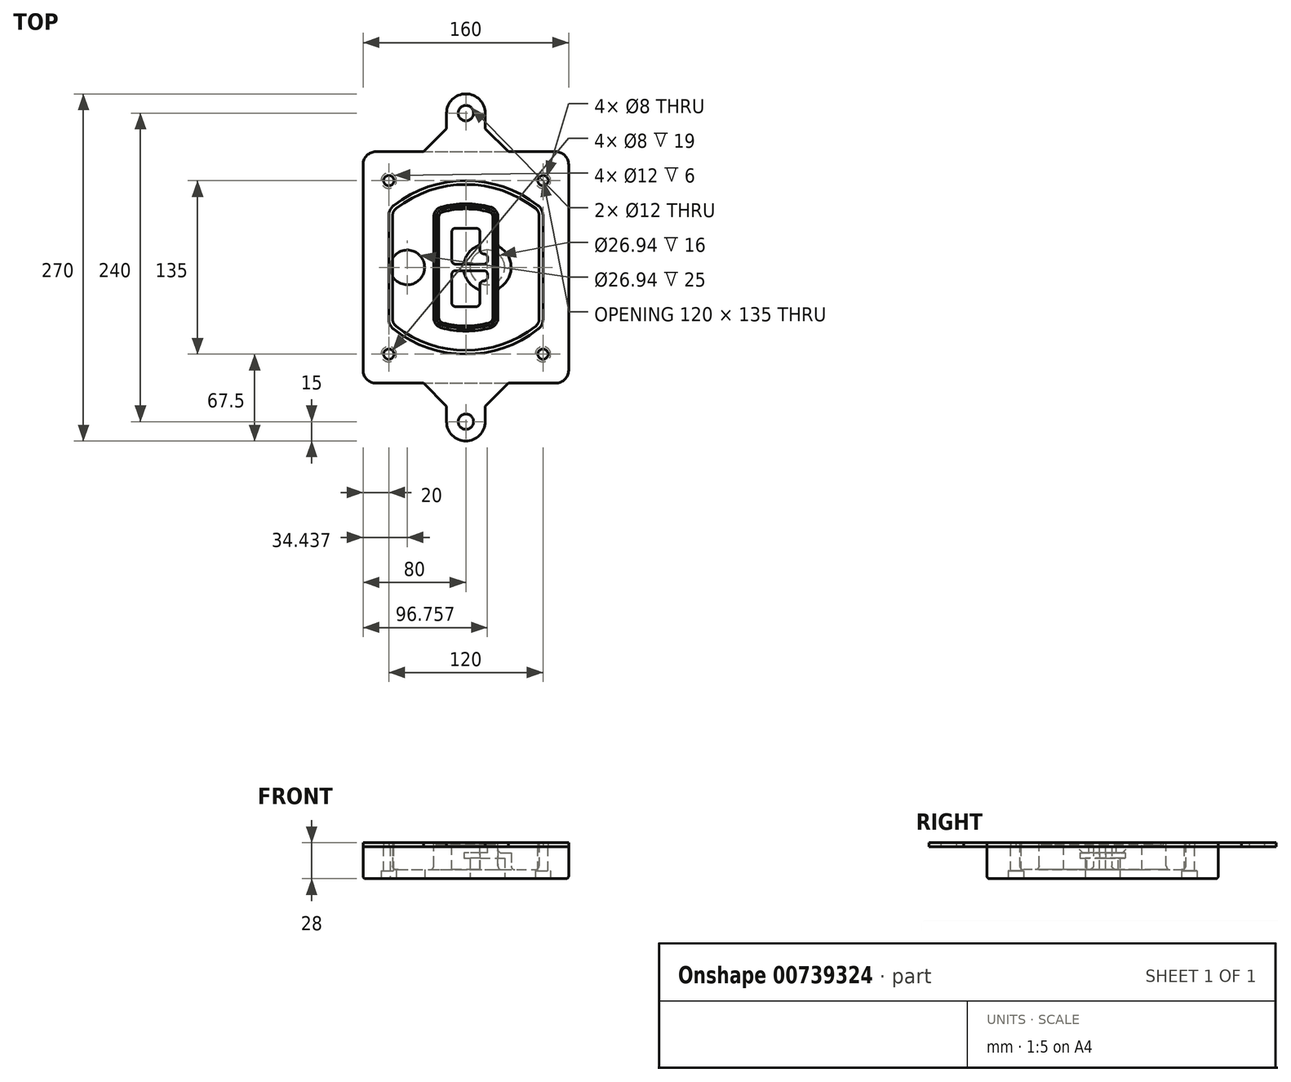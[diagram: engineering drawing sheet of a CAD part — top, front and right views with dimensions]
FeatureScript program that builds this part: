
annotation { "Feature Type Name" : "Feature", "Feature Type Description" : "" }
export const myFeature = defineFeature(function(context is Context, id is Id, definition is map)
    precondition{}
    {
        {
            var Q0;
            Q0=qCreatedBy(makeId("Top.planeOp"),FACE);
            var sketch = newSketch(context, id + "F0", { "sketchPlane" : qUnion([Q0])});
            skPoint(sketch, "E0.rect.middle", {"position": v(0, 0) * mm});
            skLineSegment(sketch, "E1.bottom", {"start": v(-70, -90) * mm, "end": v(70, -90) * mm});
            skLineSegment(sketch, "E1.top", {"start": v(-70, 90) * mm, "end": v(70, 90) * mm});
            skLineSegment(sketch, "E1.left", {"start": v(-80, -80) * mm, "end": v(-80, 80) * mm});
            skLineSegment(sketch, "E1.right", {"start": v(80, -80) * mm, "end": v(80, 80) * mm});
            skLineSegment(sketch, "E2", {"start": v(-80, 90) * mm, "end": v(80, -90) * mm, "construction": true});
            skLineSegment(sketch, "E3", {"start": v(80, 90) * mm, "end": v(-80, -90) * mm, "construction": true});
            skCircle(sketch, "E4", {"center": v(-60, 67.5) * mm, "radius": 4 * mm});
            skCircle(sketch, "E5", {"center": v(60, 67.5) * mm, "radius": 4 * mm});
            skCircle(sketch, "E6", {"center": v(60, -67.5) * mm, "radius": 4 * mm});
            skCircle(sketch, "E7", {"center": v(-60, -67.5) * mm, "radius": 4 * mm});
            skLineSegment(sketch, "E8", {"start": v(-60, 67.5) * mm, "end": v(60, 67.5) * mm, "construction": true});
            skLineSegment(sketch, "E9", {"start": v(60, 67.5) * mm, "end": v(60, -67.5) * mm, "construction": true});
            skLineSegment(sketch, "E10", {"start": v(60, -67.5) * mm, "end": v(-60, -67.5) * mm, "construction": true});
            skLineSegment(sketch, "E11", {"start": v(-60, -67.5) * mm, "end": v(-60, 67.5) * mm, "construction": true});
            skLineSegment(sketch, "E12", {"start": v(-60, 40.3) * mm, "end": v(-60, -40.3) * mm});
            skLineSegment(sketch, "E13", {"start": v(60, 40.3) * mm, "end": v(60, -40.3) * mm});
            skArc(sketch, "E14", {"start": v(56.15, 48.18) * mm, "mid": v(0, 67.5) * mm, "end": v(-56.15, 48.18) * mm});
            skArc(sketch, "E15", {"start": v(-56.15, -48.18) * mm, "mid": v(0, -67.5) * mm, "end": v(56.15, -48.18) * mm});
            skLineSegment(sketch, "E16", {"start": v(-60, 0) * mm, "end": v(60, 0) * mm, "construction": true});
            skPoint(sketch, "E17.visualSharp", {"position": v(-60, -45) * mm});
            skArc(sketch, "E17.filletArc", {"start": v(-60, -40.3) * mm, "mid": v(-58.99, -44.68) * mm, "end": v(-56.15, -48.18) * mm});
            skPoint(sketch, "E18.visualSharp", {"position": v(-60, 45) * mm});
            skArc(sketch, "E18.filletArc", {"start": v(-56.15, 48.18) * mm, "mid": v(-58.99, 44.68) * mm, "end": v(-60, 40.3) * mm});
            skPoint(sketch, "E19.visualSharp", {"position": v(60, 45) * mm});
            skArc(sketch, "E19.filletArc", {"start": v(60, 40.3) * mm, "mid": v(58.99, 44.68) * mm, "end": v(56.15, 48.18) * mm});
            skPoint(sketch, "E20.visualSharp", {"position": v(60, -45) * mm});
            skArc(sketch, "E20.filletArc", {"start": v(56.15, -48.18) * mm, "mid": v(58.99, -44.68) * mm, "end": v(60, -40.3) * mm});
            skPoint(sketch, "E21.visualSharp", {"position": v(-80, 90) * mm});
            skArc(sketch, "E21.filletArc", {"start": v(-70, 90) * mm, "mid": v(-77.07, 87.07) * mm, "end": v(-80, 80) * mm});
            skPoint(sketch, "E22.visualSharp", {"position": v(80, 90) * mm});
            skArc(sketch, "E22.filletArc", {"start": v(80, 80) * mm, "mid": v(77.07, 87.07) * mm, "end": v(70, 90) * mm});
            skPoint(sketch, "E23.visualSharp", {"position": v(80, -90) * mm});
            skArc(sketch, "E23.filletArc", {"start": v(70, -90) * mm, "mid": v(77.07, -87.07) * mm, "end": v(80, -80) * mm});
            skPoint(sketch, "E24.visualSharp", {"position": v(-80, -90) * mm});
            skArc(sketch, "E24.filletArc", {"start": v(-80, -80) * mm, "mid": v(-77.07, -87.07) * mm, "end": v(-70, -90) * mm});
            skArc(sketch, "E25.0", {"start": v(57, 40.3) * mm, "mid": v(56.3, 43.36) * mm, "end": v(54.3, 45.81) * mm});
            skLineSegment(sketch, "E25.1", {"start": v(57, 40.3) * mm, "end": v(57, -40.3) * mm});
            skArc(sketch, "E25.2", {"start": v(54.3, -45.81) * mm, "mid": v(56.3, -43.36) * mm, "end": v(57, -40.3) * mm});
            skArc(sketch, "E25.3", {"start": v(-54.3, -45.81) * mm, "mid": v(0, -64.5) * mm, "end": v(54.3, -45.81) * mm});
            skArc(sketch, "E25.4", {"start": v(-57, -40.3) * mm, "mid": v(-56.3, -43.36) * mm, "end": v(-54.3, -45.81) * mm});
            skArc(sketch, "E25.5", {"start": v(54.3, 45.81) * mm, "mid": v(0, 64.5) * mm, "end": v(-54.3, 45.81) * mm});
            skLineSegment(sketch, "E25.6", {"start": v(-57, 40.3) * mm, "end": v(-57, -40.3) * mm});
            skArc(sketch, "E25.7", {"start": v(-54.3, 45.81) * mm, "mid": v(-56.3, 43.36) * mm, "end": v(-57, 40.3) * mm});
            skArc(sketch, "E26.0", {"start": v(-58.62, 51.33) * mm, "mid": v(-62.58, 46.43) * mm, "end": v(-64, 40.3) * mm});
            skArc(sketch, "E26.1", {"start": v(58.62, 51.33) * mm, "mid": v(0, 71.5) * mm, "end": v(-58.62, 51.33) * mm});
            skArc(sketch, "E26.2", {"start": v(64, 40.3) * mm, "mid": v(62.58, 46.43) * mm, "end": v(58.62, 51.33) * mm});
            skLineSegment(sketch, "E26.3", {"start": v(64, 40.3) * mm, "end": v(64, -40.3) * mm});
            skArc(sketch, "E26.4", {"start": v(58.62, -51.33) * mm, "mid": v(62.58, -46.43) * mm, "end": v(64, -40.3) * mm});
            skLineSegment(sketch, "E26.5", {"start": v(-64, 40.3) * mm, "end": v(-64, -40.3) * mm});
            skArc(sketch, "E26.6", {"start": v(-58.62, -51.33) * mm, "mid": v(0, -71.5) * mm, "end": v(58.62, -51.33) * mm});
            skArc(sketch, "E26.7", {"start": v(-64, -40.3) * mm, "mid": v(-62.58, -46.43) * mm, "end": v(-58.62, -51.33) * mm});
            skSolve(sketch);
        }
        {
            var Q0;
            Q0=makeQuery(id+"F0.imprint","IMPRINT",FACE,{"disambiguationData":[TD([[makeQuery(id+"F0.imprint","IMPRINT",EDGE,{"derivedFrom":sQuery(id+"F0.wireOp",EDGE,"E1.bottom")}),1.0]])]});
            var Q1;
            Q1=makeQuery(id+"F0.imprint","IMPRINT",FACE,{"disambiguationData":[TD([[makeQuery(id+"F0.imprint","IMPRINT",EDGE,{"derivedFrom":sQuery(id+"F0.wireOp",EDGE,"E12")}),1.0]])]});
            var Q2;
            Q2=makeQuery(id+"F0.imprint","IMPRINT",FACE,{"disambiguationData":[TD([[makeQuery(id+"F0.imprint","IMPRINT",EDGE,{"derivedFrom":sQuery(id+"F0.wireOp",EDGE,"E25.0")}),1.0]])]});
            var Q3;
            Q3=makeQuery(id+"F0.imprint","IMPRINT",FACE,{"disambiguationData":[TD([[makeQuery(id+"F0.imprint","IMPRINT",EDGE,{"derivedFrom":sQuery(id+"F0.wireOp",EDGE,"E12")}),-1.0]])]});
            extrude(context, id + "F1", {"entities" : qUnion([Q0, Q1, Q2, Q3]), "oppositeDirection" : true, "depth" : 25 * mm});
        }
        {
            var Q0;
            Q0=makeQuery(id+"F0.imprint","IMPRINT",FACE,{"disambiguationData":[TD([[makeQuery(id+"F0.imprint","IMPRINT",EDGE,{"derivedFrom":sQuery(id+"F0.wireOp",EDGE,"E12")}),1.0]])]});
            extrude(context, id + "F2", {"entities" : qUnion([Q0]), "operationType" : NewBodyOperationType.ADD, "depth" : 3 * mm});
        }
        {
            var Q0;
            Q0=makeQuery(id+"F0.imprint","IMPRINT",FACE,{"disambiguationData":[TD([[makeQuery(id+"F0.imprint","IMPRINT",EDGE,{"derivedFrom":sQuery(id+"F0.wireOp",EDGE,"E25.0")}),1.0]])]});
            extrude(context, id + "F3", {"entities" : qUnion([Q0]), "operationType" : NewBodyOperationType.REMOVE, "oppositeDirection" : true, "depth" : 18 * mm});
        }
        {
            var Q0;
            Q0=makeQuery(id+"F2.opExtrude","CAP_FACE",FACE,{"disambiguationData":[OSD([sQuery(id+"F0.wireOp",EDGE,"E12"),sQuery(id+"F0.wireOp",EDGE,"E13"),sQuery(id+"F0.wireOp",EDGE,"E14"),sQuery(id+"F0.wireOp",EDGE,"E15"),sQuery(id+"F0.wireOp",EDGE,"E17.filletArc"),sQuery(id+"F0.wireOp",EDGE,"E18.filletArc"),sQuery(id+"F0.wireOp",EDGE,"E19.filletArc"),sQuery(id+"F0.wireOp",EDGE,"E20.filletArc"),sQuery(id+"F0.wireOp",EDGE,"E25.0"),sQuery(id+"F0.wireOp",EDGE,"E25.1"),sQuery(id+"F0.wireOp",EDGE,"E25.2"),sQuery(id+"F0.wireOp",EDGE,"E25.3"),sQuery(id+"F0.wireOp",EDGE,"E25.4"),sQuery(id+"F0.wireOp",EDGE,"E25.5"),sQuery(id+"F0.wireOp",EDGE,"E25.6"),sQuery(id+"F0.wireOp",EDGE,"E25.7")])],"isStart":false});
            var sketch = newSketch(context, id + "F4", { "sketchPlane" : qUnion([Q0])});
            skArc(sketch, "E27.0", {"start": v(-19.08, -46.97) * mm, "mid": v(0, -49.5) * mm, "end": v(19.08, -46.97) * mm});
            skArc(sketch, "E28.0", {"start": v(19.08, 46.97) * mm, "mid": v(0, 49.5) * mm, "end": v(-19.08, 46.97) * mm});
            skLineSegment(sketch, "E29", {"start": v(-25, 39.25) * mm, "end": v(-25, -39.25) * mm});
            skLineSegment(sketch, "E30", {"start": v(25, 39.25) * mm, "end": v(25, -39.25) * mm});
            skLineSegment(sketch, "E31", {"start": v(-25, 45.1) * mm, "end": v(25, 45.1) * mm, "construction": true});
            skLineSegment(sketch, "E32", {"start": v(-25, -45.1) * mm, "end": v(25, -45.1) * mm, "construction": true});
            skPoint(sketch, "E33.visualSharp", {"position": v(-25, 45.1) * mm});
            skArc(sketch, "E33.filletArc", {"start": v(-19.08, 46.97) * mm, "mid": v(-23.35, 44.11) * mm, "end": v(-25, 39.25) * mm});
            skPoint(sketch, "E34.visualSharp", {"position": v(25, 45.1) * mm});
            skArc(sketch, "E34.filletArc", {"start": v(25, 39.25) * mm, "mid": v(23.35, 44.11) * mm, "end": v(19.08, 46.97) * mm});
            skPoint(sketch, "E35.visualSharp", {"position": v(25, -45.1) * mm});
            skArc(sketch, "E35.filletArc", {"start": v(19.08, -46.97) * mm, "mid": v(23.35, -44.11) * mm, "end": v(25, -39.25) * mm});
            skPoint(sketch, "E36.visualSharp", {"position": v(-25, -45.1) * mm});
            skArc(sketch, "E36.filletArc", {"start": v(-25, -39.25) * mm, "mid": v(-23.35, -44.11) * mm, "end": v(-19.08, -46.97) * mm});
            skArc(sketch, "E37.0", {"start": v(54.3, 45.81) * mm, "mid": v(0, 64.5) * mm, "end": v(-54.3, 45.81) * mm});
            skArc(sketch, "E37.1", {"start": v(-54.3, 45.81) * mm, "mid": v(-56.3, 43.36) * mm, "end": v(-57, 40.3) * mm});
            skLineSegment(sketch, "E37.2", {"start": v(-57, 40.3) * mm, "end": v(-57, -40.3) * mm});
            skArc(sketch, "E37.3", {"start": v(-57, -40.3) * mm, "mid": v(-56.3, -43.36) * mm, "end": v(-54.3, -45.81) * mm});
            skArc(sketch, "E37.4", {"start": v(-54.3, -45.81) * mm, "mid": v(0, -64.5) * mm, "end": v(54.3, -45.81) * mm});
            skArc(sketch, "E37.5", {"start": v(54.3, -45.81) * mm, "mid": v(56.3, -43.36) * mm, "end": v(57, -40.3) * mm});
            skLineSegment(sketch, "E37.6", {"start": v(57, 40.3) * mm, "end": v(57, -40.3) * mm});
            skArc(sketch, "E37.7", {"start": v(57, 40.3) * mm, "mid": v(56.3, 43.36) * mm, "end": v(54.3, 45.81) * mm});
            skLineSegment(sketch, "E38.0", {"start": v(23, 39.25) * mm, "end": v(23, -39.25) * mm});
            skArc(sketch, "E38.1", {"start": v(18.56, -45.04) * mm, "mid": v(21.76, -42.9) * mm, "end": v(23, -39.25) * mm});
            skArc(sketch, "E38.2", {"start": v(-18.56, -45.04) * mm, "mid": v(0, -47.5) * mm, "end": v(18.56, -45.04) * mm});
            skArc(sketch, "E38.3", {"start": v(-23, -39.25) * mm, "mid": v(-21.76, -42.9) * mm, "end": v(-18.56, -45.04) * mm});
            skLineSegment(sketch, "E38.4", {"start": v(-23, 39.25) * mm, "end": v(-23, -39.25) * mm});
            skArc(sketch, "E38.5", {"start": v(23, 39.25) * mm, "mid": v(21.76, 42.9) * mm, "end": v(18.56, 45.04) * mm});
            skArc(sketch, "E38.6", {"start": v(-18.56, 45.04) * mm, "mid": v(-21.76, 42.9) * mm, "end": v(-23, 39.25) * mm});
            skArc(sketch, "E38.7", {"start": v(18.56, 45.04) * mm, "mid": v(0, 47.5) * mm, "end": v(-18.56, 45.04) * mm});
            skArc(sketch, "E39.0", {"start": v(21, 39.25) * mm, "mid": v(20.18, 41.68) * mm, "end": v(18.04, 43.1) * mm});
            skLineSegment(sketch, "E39.1", {"start": v(21, 39.25) * mm, "end": v(21, -39.25) * mm});
            skArc(sketch, "E39.2", {"start": v(18.04, -43.1) * mm, "mid": v(20.18, -41.68) * mm, "end": v(21, -39.25) * mm});
            skArc(sketch, "E39.3", {"start": v(-18.04, -43.1) * mm, "mid": v(0, -45.5) * mm, "end": v(18.04, -43.1) * mm});
            skArc(sketch, "E39.4", {"start": v(-21, -39.25) * mm, "mid": v(-20.18, -41.68) * mm, "end": v(-18.04, -43.1) * mm});
            skArc(sketch, "E39.5", {"start": v(18.04, 43.1) * mm, "mid": v(0, 45.5) * mm, "end": v(-18.04, 43.1) * mm});
            skLineSegment(sketch, "E39.6", {"start": v(-21, 39.25) * mm, "end": v(-21, -39.25) * mm});
            skArc(sketch, "E39.7", {"start": v(-18.04, 43.1) * mm, "mid": v(-20.18, 41.68) * mm, "end": v(-21, 39.25) * mm});
            skLineSegment(sketch, "E40", {"start": v(-25, 0) * mm, "end": v(25, 0) * mm, "construction": true});
            skLineSegment(sketch, "E41", {"start": v(-11, 5.5) * mm, "end": v(-11, 27.5) * mm});
            skLineSegment(sketch, "E42", {"start": v(-8, 30.5) * mm, "end": v(8, 30.5) * mm});
            skLineSegment(sketch, "E43", {"start": v(11, 27.5) * mm, "end": v(11, 13.5) * mm});
            skLineSegment(sketch, "E44", {"start": v(14, 10.5) * mm, "end": v(14, 10.5) * mm});
            skLineSegment(sketch, "E45", {"start": v(17, 7.5) * mm, "end": v(17, 5.5) * mm});
            skLineSegment(sketch, "E46", {"start": v(14, 2.5) * mm, "end": v(-8, 2.5) * mm});
            skPoint(sketch, "E47.visualSharp", {"position": v(-11, 30.5) * mm});
            skArc(sketch, "E47.filletArc", {"start": v(-8, 30.5) * mm, "mid": v(-10.12, 29.62) * mm, "end": v(-11, 27.5) * mm});
            skPoint(sketch, "E48.visualSharp", {"position": v(11, 30.5) * mm});
            skArc(sketch, "E48.filletArc", {"start": v(11, 27.5) * mm, "mid": v(10.12, 29.62) * mm, "end": v(8, 30.5) * mm});
            skPoint(sketch, "E49.visualSharp", {"position": v(11, 10.5) * mm});
            skArc(sketch, "E49.filletArc", {"start": v(11, 13.5) * mm, "mid": v(11.88, 11.38) * mm, "end": v(14, 10.5) * mm});
            skPoint(sketch, "E50.visualSharp", {"position": v(17, 10.5) * mm});
            skArc(sketch, "E50.filletArc", {"start": v(17, 7.5) * mm, "mid": v(16.12, 9.62) * mm, "end": v(14, 10.5) * mm});
            skPoint(sketch, "E51.visualSharp", {"position": v(17, 2.5) * mm});
            skArc(sketch, "E51.filletArc", {"start": v(14, 2.5) * mm, "mid": v(16.12, 3.38) * mm, "end": v(17, 5.5) * mm});
            skPoint(sketch, "E52.visualSharp", {"position": v(-11, 2.5) * mm});
            skArc(sketch, "E52.filletArc", {"start": v(-11, 5.5) * mm, "mid": v(-10.12, 3.38) * mm, "end": v(-8, 2.5) * mm});
            skLineSegment(sketch, "E53.0.MirrorCS", {"start": v(14, -2.5) * mm, "end": v(-8, -2.5) * mm});
            skArc(sketch, "E54.0.MirrorCS", {"start": v(-11, -5.5) * mm, "mid": v(-10.12, -3.38) * mm, "end": v(-8, -2.5) * mm});
            skLineSegment(sketch, "E55.0.MirrorCS", {"start": v(-11, -5.5) * mm, "end": v(-11, -27.5) * mm});
            skArc(sketch, "E56.0.MirrorCS", {"start": v(-8, -30.5) * mm, "mid": v(-10.12, -29.62) * mm, "end": v(-11, -27.5) * mm});
            skLineSegment(sketch, "E57.0.MirrorCS", {"start": v(-8, -30.5) * mm, "end": v(8, -30.5) * mm});
            skArc(sketch, "E58.0.MirrorCS", {"start": v(11, -27.5) * mm, "mid": v(10.12, -29.62) * mm, "end": v(8, -30.5) * mm});
            skLineSegment(sketch, "E59.0.MirrorCS", {"start": v(11, -27.5) * mm, "end": v(11, -13.5) * mm});
            skArc(sketch, "E60.0.MirrorCS", {"start": v(11, -13.5) * mm, "mid": v(11.88, -11.38) * mm, "end": v(14, -10.5) * mm});
            skArc(sketch, "E61.0.MirrorCS", {"start": v(17, -7.5) * mm, "mid": v(16.12, -9.62) * mm, "end": v(14, -10.5) * mm});
            skLineSegment(sketch, "E62.0.MirrorCS", {"start": v(17, -7.5) * mm, "end": v(17, -5.5) * mm});
            skArc(sketch, "E63.0.MirrorCS", {"start": v(14, -2.5) * mm, "mid": v(16.12, -3.38) * mm, "end": v(17, -5.5) * mm});
            skSolve(sketch);
        }
        {
            var Q0;
            Q0=makeQuery(id+"F4.imprint","IMPRINT",FACE,{"disambiguationData":[TD([[makeQuery(id+"F4.imprint","IMPRINT",EDGE,{"derivedFrom":sQuery(id+"F4.wireOp",EDGE,"E27.0")}),1.0]])]});
            var Q1;
            Q1=makeQuery(id+"F4.imprint","IMPRINT",FACE,{"disambiguationData":[TD([[makeQuery(id+"F4.imprint","IMPRINT",EDGE,{"derivedFrom":sQuery(id+"F4.wireOp",EDGE,"E38.0")}),-1.0]])]});
            var Q2;
            Q2=makeQuery(id+"F4.imprint","IMPRINT",FACE,{"disambiguationData":[TD([[makeQuery(id+"F4.imprint","IMPRINT",EDGE,{"derivedFrom":sQuery(id+"F4.wireOp",EDGE,"E39.0")}),1.0]])]});
            extrude(context, id + "F5", {"entities" : qUnion([Q0, Q1, Q2]), "operationType" : NewBodyOperationType.ADD, "endBound" : BoundingType.UP_TO_NEXT, "oppositeDirection" : true, "depth" : 25 * mm});
        }
        {
            var Q0;
            Q0=makeQuery(id+"F4.imprint","IMPRINT",FACE,{"disambiguationData":[TD([[makeQuery(id+"F4.imprint","IMPRINT",EDGE,{"derivedFrom":sQuery(id+"F4.wireOp",EDGE,"E38.0")}),-1.0]])]});
            extrude(context, id + "F6", {"entities" : qUnion([Q0]), "operationType" : NewBodyOperationType.REMOVE, "oppositeDirection" : true, "depth" : 2 * mm});
        }
        {
            var Q0;
            Q0=makeQuery(id+"F1.opExtrude","CAP_FACE",FACE,{"disambiguationData":[OSD([sQuery(id+"F0.wireOp",EDGE,"E1.bottom"),sQuery(id+"F0.wireOp",EDGE,"E1.top"),sQuery(id+"F0.wireOp",EDGE,"E1.left"),sQuery(id+"F0.wireOp",EDGE,"E1.right"),sQuery(id+"F0.wireOp",EDGE,"E4"),sQuery(id+"F0.wireOp",EDGE,"E5"),sQuery(id+"F0.wireOp",EDGE,"E6"),sQuery(id+"F0.wireOp",EDGE,"E7"),sQuery(id+"F0.wireOp",EDGE,"E21.filletArc"),sQuery(id+"F0.wireOp",EDGE,"E22.filletArc"),sQuery(id+"F0.wireOp",EDGE,"E23.filletArc"),sQuery(id+"F0.wireOp",EDGE,"E24.filletArc")])],"isStart":false});
            var sketch = newSketch(context, id + "F7", { "sketchPlane" : qUnion([Q0])});
            skCircle(sketch, "E64", {"center": v(16.76, 0) * mm, "radius": 13.47 * mm});
            skCircle(sketch, "E65", {"center": v(-45.56, 0) * mm, "radius": 13.47 * mm});
            skLineSegment(sketch, "E66", {"start": v(80, 0) * mm, "end": v(-80, 0) * mm});
            skCircle(sketch, "E67", {"center": v(16.76, 0) * mm, "radius": 18.47 * mm});
            skCircle(sketch, "E68", {"center": v(60, -67.5) * mm, "radius": 6 * mm});
            skCircle(sketch, "E69", {"center": v(-60, -67.5) * mm, "radius": 6 * mm});
            skCircle(sketch, "E70", {"center": v(-60, 67.5) * mm, "radius": 6 * mm});
            skCircle(sketch, "E71", {"center": v(60, 67.5) * mm, "radius": 6 * mm});
            skSolve(sketch);
        }
        {
            var Q0;
            {var subQ1=sQuery(id+"F7.wireOp",EDGE,"E66");var subQ4=sQuery(id+"F7.wireOp",EDGE,"E64");var subQ6=makeQuery(id+"F7.imprint","INTERSECT",VERTEX,{"disambiguationData":[OD(0.0)],"derivedFrom":[subQ4,subQ1]});Q0=makeQuery(id+"F7.imprint","IMPRINT",FACE,{"disambiguationData":[TD([[makeQuery(id+"F7.imprint","IMPRINT",EDGE,{"disambiguationData":[TD([[subQ6,-1.0]])],"derivedFrom":subQ4}),-1.0]])]});}
            var Q1;
            {var subQ0=sQuery(id+"F7.wireOp",EDGE,"E66");var subQ1=sQuery(id+"F7.wireOp",EDGE,"E64");var subQ3=makeQuery(id+"F7.imprint","INTERSECT",VERTEX,{"disambiguationData":[OD(0.0)],"derivedFrom":[subQ1,subQ0]});Q1=makeQuery(id+"F7.imprint","IMPRINT",FACE,{"disambiguationData":[TD([[makeQuery(id+"F7.imprint","IMPRINT",EDGE,{"disambiguationData":[TD([[subQ3,-1.0]])],"derivedFrom":subQ1}),1.0]])]});}
            var Q2;
            {var subQ0=sQuery(id+"F7.wireOp",EDGE,"E66");var subQ1=sQuery(id+"F7.wireOp",EDGE,"E64");var subQ3=makeQuery(id+"F7.imprint","INTERSECT",VERTEX,{"disambiguationData":[OD(0.0)],"derivedFrom":[subQ1,subQ0]});Q2=makeQuery(id+"F7.imprint","IMPRINT",FACE,{"disambiguationData":[TD([[makeQuery(id+"F7.imprint","IMPRINT",EDGE,{"disambiguationData":[TD([[subQ3,1.0]])],"derivedFrom":subQ1}),1.0]])]});}
            var Q3;
            {var subQ1=sQuery(id+"F7.wireOp",EDGE,"E66");var subQ4=sQuery(id+"F7.wireOp",EDGE,"E64");var subQ6=makeQuery(id+"F7.imprint","INTERSECT",VERTEX,{"disambiguationData":[OD(0.0)],"derivedFrom":[subQ4,subQ1]});Q3=makeQuery(id+"F7.imprint","IMPRINT",FACE,{"disambiguationData":[TD([[makeQuery(id+"F7.imprint","IMPRINT",EDGE,{"disambiguationData":[TD([[subQ6,1.0]])],"derivedFrom":subQ4}),-1.0]])]});}
            extrude(context, id + "F8", {"entities" : qUnion([Q0, Q1, Q2, Q3]), "operationType" : NewBodyOperationType.ADD, "oppositeDirection" : true, "depth" : 20 * mm});
        }
        {
            var Q0;
            {var subQ0=sQuery(id+"F7.wireOp",EDGE,"E66");var subQ1=sQuery(id+"F7.wireOp",EDGE,"E64");var subQ3=makeQuery(id+"F7.imprint","INTERSECT",VERTEX,{"disambiguationData":[OD(0.0)],"derivedFrom":[subQ1,subQ0]});Q0=makeQuery(id+"F7.imprint","IMPRINT",FACE,{"disambiguationData":[TD([[makeQuery(id+"F7.imprint","IMPRINT",EDGE,{"disambiguationData":[TD([[subQ3,-1.0]])],"derivedFrom":subQ1}),1.0]])]});}
            var Q1;
            {var subQ0=sQuery(id+"F7.wireOp",EDGE,"E66");var subQ1=sQuery(id+"F7.wireOp",EDGE,"E64");var subQ3=makeQuery(id+"F7.imprint","INTERSECT",VERTEX,{"disambiguationData":[OD(0.0)],"derivedFrom":[subQ1,subQ0]});Q1=makeQuery(id+"F7.imprint","IMPRINT",FACE,{"disambiguationData":[TD([[makeQuery(id+"F7.imprint","IMPRINT",EDGE,{"disambiguationData":[TD([[subQ3,1.0]])],"derivedFrom":subQ1}),1.0]])]});}
            extrude(context, id + "F9", {"entities" : qUnion([Q0, Q1]), "operationType" : NewBodyOperationType.REMOVE, "oppositeDirection" : true, "depth" : 16 * mm});
        }
        {
            var Q0;
            {var subQ0=sQuery(id+"F7.wireOp",EDGE,"E66");var subQ1=sQuery(id+"F7.wireOp",EDGE,"E65");var subQ3=makeQuery(id+"F7.imprint","INTERSECT",VERTEX,{"disambiguationData":[OD(0.0)],"derivedFrom":[subQ1,subQ0]});Q0=makeQuery(id+"F7.imprint","IMPRINT",FACE,{"disambiguationData":[TD([[makeQuery(id+"F7.imprint","IMPRINT",EDGE,{"disambiguationData":[TD([[subQ3,-1.0]])],"derivedFrom":subQ1}),1.0]])]});}
            var Q1;
            {var subQ0=sQuery(id+"F7.wireOp",EDGE,"E66");var subQ1=sQuery(id+"F7.wireOp",EDGE,"E65");var subQ3=makeQuery(id+"F7.imprint","INTERSECT",VERTEX,{"disambiguationData":[OD(0.0)],"derivedFrom":[subQ1,subQ0]});Q1=makeQuery(id+"F7.imprint","IMPRINT",FACE,{"disambiguationData":[TD([[makeQuery(id+"F7.imprint","IMPRINT",EDGE,{"disambiguationData":[TD([[subQ3,1.0]])],"derivedFrom":subQ1}),1.0]])]});}
            extrude(context, id + "F10", {"entities" : qUnion([Q0, Q1]), "operationType" : NewBodyOperationType.REMOVE, "oppositeDirection" : true, "depth" : 25 * mm});
        }
        {
            var Q0;
            Q0=makeQuery(id+"F7.imprint","IMPRINT",FACE,{"disambiguationData":[TD([[makeQuery(id+"F7.imprint","IMPRINT",EDGE,{"derivedFrom":sQuery(id+"F7.wireOp",EDGE,"E68")}),1.0]])]});
            var Q1;
            Q1=makeQuery(id+"F7.imprint","IMPRINT",FACE,{"disambiguationData":[TD([[makeQuery(id+"F7.imprint","IMPRINT",EDGE,{"derivedFrom":makeQuery(id+"F1.opExtrude","CAP_EDGE",EDGE,{"disambiguationData":[OSD([sQuery(id+"F0.wireOp",EDGE,"E5")])],"isStart":false})}),-1.0]])]});
            var Q2;
            Q2=makeQuery(id+"F7.imprint","IMPRINT",FACE,{"disambiguationData":[TD([[makeQuery(id+"F7.imprint","IMPRINT",EDGE,{"derivedFrom":sQuery(id+"F7.wireOp",EDGE,"E69")}),1.0]])]});
            var Q3;
            Q3=makeQuery(id+"F7.imprint","IMPRINT",FACE,{"disambiguationData":[TD([[makeQuery(id+"F7.imprint","IMPRINT",EDGE,{"derivedFrom":makeQuery(id+"F1.opExtrude","CAP_EDGE",EDGE,{"disambiguationData":[OSD([sQuery(id+"F0.wireOp",EDGE,"E4")])],"isStart":false})}),-1.0]])]});
            var Q4;
            Q4=makeQuery(id+"F7.imprint","IMPRINT",FACE,{"disambiguationData":[TD([[makeQuery(id+"F7.imprint","IMPRINT",EDGE,{"derivedFrom":sQuery(id+"F7.wireOp",EDGE,"E70")}),1.0]])]});
            var Q5;
            Q5=makeQuery(id+"F7.imprint","IMPRINT",FACE,{"disambiguationData":[TD([[makeQuery(id+"F7.imprint","IMPRINT",EDGE,{"derivedFrom":makeQuery(id+"F1.opExtrude","CAP_EDGE",EDGE,{"disambiguationData":[OSD([sQuery(id+"F0.wireOp",EDGE,"E7")])],"isStart":false})}),-1.0]])]});
            var Q6;
            Q6=makeQuery(id+"F7.imprint","IMPRINT",FACE,{"disambiguationData":[TD([[makeQuery(id+"F7.imprint","IMPRINT",EDGE,{"derivedFrom":sQuery(id+"F7.wireOp",EDGE,"E71")}),1.0]])]});
            var Q7;
            Q7=makeQuery(id+"F7.imprint","IMPRINT",FACE,{"disambiguationData":[TD([[makeQuery(id+"F7.imprint","IMPRINT",EDGE,{"derivedFrom":makeQuery(id+"F1.opExtrude","CAP_EDGE",EDGE,{"disambiguationData":[OSD([sQuery(id+"F0.wireOp",EDGE,"E6")])],"isStart":false})}),-1.0]])]});
            extrude(context, id + "F11", {"entities" : qUnion([Q0, Q1, Q2, Q3, Q4, Q5, Q6, Q7]), "operationType" : NewBodyOperationType.REMOVE, "oppositeDirection" : true, "depth" : 6 * mm});
        }
        {
            var Q0;
            Q0=makeQuery(id+"F9.boolean.opBoolean","COPY",FACE,{"derivedFrom":makeQuery(id+"F9.opExtrude","CAP_FACE",FACE,{"disambiguationData":[OSD([sQuery(id+"F7.wireOp",EDGE,"E64")])],"isStart":false})});
            var sketch = newSketch(context, id + "F12", { "sketchPlane" : qUnion([Q0])});
            skArc(sketch, "E72.0", {"start": v(11, 17.55) * mm, "mid": v(2.57, 11.82) * mm, "end": v(-1.54, 2.5) * mm});
            skArc(sketch, "E72.1", {"start": v(-1.54, -2.5) * mm, "mid": v(2.57, -11.82) * mm, "end": v(11, -17.55) * mm});
            skLineSegment(sketch, "E73", {"start": v(-1.54, -2.5) * mm, "end": v(14, -2.5) * mm});
            skLineSegment(sketch, "E74.0", {"start": v(14, 2.5) * mm, "end": v(-1.54, 2.5) * mm});
            skArc(sketch, "E74.1", {"start": v(14, 2.5) * mm, "mid": v(16.12, 3.38) * mm, "end": v(17, 5.5) * mm});
            skLineSegment(sketch, "E74.2", {"start": v(17, 7.5) * mm, "end": v(17, 5.5) * mm});
            skArc(sketch, "E74.3", {"start": v(17, 7.5) * mm, "mid": v(16.12, 9.62) * mm, "end": v(14, 10.5) * mm});
            skArc(sketch, "E74.4", {"start": v(11, 13.5) * mm, "mid": v(11.88, 11.38) * mm, "end": v(14, 10.5) * mm});
            skLineSegment(sketch, "E74.5", {"start": v(11, 17.55) * mm, "end": v(11, 13.5) * mm});
            skLineSegment(sketch, "E74.7", {"start": v(14, -2.5) * mm, "end": v(-1.54, -2.5) * mm});
            skArc(sketch, "E74.8", {"start": v(14, -2.5) * mm, "mid": v(16.12, -3.38) * mm, "end": v(17, -5.5) * mm});
            skLineSegment(sketch, "E74.9", {"start": v(17, -7.5) * mm, "end": v(17, -5.5) * mm});
            skArc(sketch, "E74.10", {"start": v(17, -7.5) * mm, "mid": v(16.12, -9.62) * mm, "end": v(14, -10.5) * mm});
            skArc(sketch, "E74.11", {"start": v(11, -13.5) * mm, "mid": v(11.88, -11.38) * mm, "end": v(14, -10.5) * mm});
            skLineSegment(sketch, "E74.12", {"start": v(11, -17.55) * mm, "end": v(11, -13.5) * mm});
            skPoint(sketch, "E75.orphan", {"position": v(11, -27.5) * mm});
            skPoint(sketch, "E76.orphan", {"position": v(-8, -2.5) * mm});
            skPoint(sketch, "E77.orphan", {"position": v(-8, 2.5) * mm});
            skPoint(sketch, "E78.orphan", {"position": v(11, 27.5) * mm});
            skSolve(sketch);
        }
        {
            var Q0;
            {var subQ7=sQuery(id+"F12.wireOp",EDGE,"E72.0");var subQ14=sQuery(id+"F12.wireOp",EDGE,"E72.1");var subQ16=sQuery(id+"F12.wireOp",EDGE,"E74.1");var subQ18=sQuery(id+"F12.wireOp",EDGE,"E74.8");Q0=qUnion([makeQuery(id+"F12.imprint","IMPRINT",FACE,{"disambiguationData":[TD([[makeQuery(id+"F12.imprint","IMPRINT",EDGE,{"derivedFrom":subQ7}),1.0]])]}),makeQuery(id+"F12.imprint","IMPRINT",FACE,{"disambiguationData":[TD([[makeQuery(id+"F12.imprint","IMPRINT",EDGE,{"derivedFrom":subQ14}),1.0]])]}),makeQuery(id+"F12.imprint","IMPRINT",FACE,{"disambiguationData":[TD([[makeQuery(id+"F12.imprint","IMPRINT",EDGE,{"derivedFrom":subQ16}),1.0]])]}),makeQuery(id+"F12.imprint","IMPRINT",FACE,{"disambiguationData":[TD([[makeQuery(id+"F12.imprint","IMPRINT",EDGE,{"derivedFrom":subQ18}),-1.0]])]})]);}
            var Q1;
            Q1=makeQuery(id+"F5.boolean.opBoolean","SPLIT",FACE,{"disambiguationData":[TD([makeQuery(id+"F5.opExtrude","SWEPT_FACE",FACE,{"disambiguationData":[OSD([sQuery(id+"F4.wireOp",EDGE,"E41")])]})])],"derivedFrom":makeQuery(id+"F3.boolean.opBoolean","COPY",FACE,{"derivedFrom":makeQuery(id+"F3.opExtrude","CAP_FACE",FACE,{"disambiguationData":[OSD([sQuery(id+"F0.wireOp",EDGE,"E25.0"),sQuery(id+"F0.wireOp",EDGE,"E25.1"),sQuery(id+"F0.wireOp",EDGE,"E25.2"),sQuery(id+"F0.wireOp",EDGE,"E25.3"),sQuery(id+"F0.wireOp",EDGE,"E25.4"),sQuery(id+"F0.wireOp",EDGE,"E25.5"),sQuery(id+"F0.wireOp",EDGE,"E25.6"),sQuery(id+"F0.wireOp",EDGE,"E25.7")])],"isStart":false})})});
            extrude(context, id + "F13", {"entities" : qUnion([Q0]), "operationType" : NewBodyOperationType.REMOVE, "endBound" : BoundingType.UP_TO_SURFACE, "endBoundEntityFace" : qUnion([Q1]), "depth" : 25 * mm});
        }
        {
            var Q0;
            Q0=makeQuery(id+"F3.boolean.opBoolean","COPY",EDGE,{"derivedFrom":makeQuery(id+"F3.opExtrude","CAP_EDGE",EDGE,{"disambiguationData":[OSD([sQuery(id+"F0.wireOp",EDGE,"E25.6")])],"isStart":false})});
            var Q1;
            Q1=makeQuery(id+"F8.boolean.opBoolean","INTERSECT",EDGE,{"derivedFrom":[makeQuery(id+"F5.opExtrude","SWEPT_FACE",FACE,{"disambiguationData":[OSD([sQuery(id+"F4.wireOp",EDGE,"E30")])]}),makeQuery(id+"F8.opExtrude","CAP_FACE",FACE,{"disambiguationData":[OSD([sQuery(id+"F7.wireOp",EDGE,"E67")])],"isStart":false})]});
            var Q2;
            Q2=makeQuery(id+"F8.boolean.opBoolean","INTERSECT",EDGE,{"disambiguationData":[OD(1.0)],"derivedFrom":[makeQuery(id+"F5.opExtrude","SWEPT_FACE",FACE,{"disambiguationData":[OSD([sQuery(id+"F4.wireOp",EDGE,"E30")])]}),makeQuery(id+"F8.opExtrude","SWEPT_FACE",FACE,{"disambiguationData":[OSD([sQuery(id+"F7.wireOp",EDGE,"E67")])]})]});
            var Q3;
            {var subQ0=sQuery(id+"F4.wireOp",EDGE,"E30");Q3=makeQuery(id+"F8.boolean.opBoolean","SPLIT",EDGE,{"disambiguationData":[TD([makeQuery(id+"F5.opExtrude","SWEPT_FACE",FACE,{"disambiguationData":[OSD([sQuery(id+"F4.wireOp",EDGE,"E35.filletArc")])]})])],"derivedFrom":makeQuery(id+"F5.opExtrude","CAP_EDGE",EDGE,{"disambiguationData":[OSD([subQ0])],"isStart":false})});}
            var Q4;
            {var subQ0=sQuery(id+"F0.wireOp",EDGE,"E25.7");var subQ1=sQuery(id+"F0.wireOp",EDGE,"E25.1");var subQ2=sQuery(id+"F0.wireOp",EDGE,"E25.6");var subQ3=sQuery(id+"F0.wireOp",EDGE,"E25.5");var subQ4=sQuery(id+"F0.wireOp",EDGE,"E25.4");var subQ5=sQuery(id+"F0.wireOp",EDGE,"E25.0");var subQ6=sQuery(id+"F0.wireOp",EDGE,"E25.2");var subQ7=sQuery(id+"F0.wireOp",EDGE,"E25.3");Q4=makeQuery(id+"F8.boolean.opBoolean","INTERSECT",EDGE,{"derivedFrom":[makeQuery(id+"F5.boolean.opBoolean","SPLIT",FACE,{"disambiguationData":[TD([makeQuery(id+"F2.opExtrude","SWEPT_FACE",FACE,{"disambiguationData":[OSD([subQ5])]})])],"derivedFrom":makeQuery(id+"F3.boolean.opBoolean","COPY",FACE,{"derivedFrom":makeQuery(id+"F3.opExtrude","CAP_FACE",FACE,{"disambiguationData":[OSD([subQ5,subQ1,subQ6,subQ7,subQ4,subQ3,subQ2,subQ0])],"isStart":false})})}),makeQuery(id+"F8.opExtrude","SWEPT_FACE",FACE,{"disambiguationData":[OSD([sQuery(id+"F7.wireOp",EDGE,"E67")])]})]});}
            var Q5;
            Q5=makeQuery(id+"F8.boolean.opBoolean","INTERSECT",EDGE,{"disambiguationData":[OD(0.0)],"derivedFrom":[makeQuery(id+"F5.opExtrude","SWEPT_FACE",FACE,{"disambiguationData":[OSD([sQuery(id+"F4.wireOp",EDGE,"E30")])]}),makeQuery(id+"F8.opExtrude","SWEPT_FACE",FACE,{"disambiguationData":[OSD([sQuery(id+"F7.wireOp",EDGE,"E67")])]})]});
            fillet(context, id + "F14", {"entities" : qUnion([Q0, Q1, Q2, Q3, Q4, Q5]), "radius" : 3 * mm, "tangentPropagation" : true, "allowEdgeOverflow" : false});
        }
        {
            var Q0;
            Q0=makeQuery(id+"F1.opExtrude","CAP_EDGE",EDGE,{"disambiguationData":[OSD([sQuery(id+"F0.wireOp",EDGE,"E1.bottom")])],"isStart":false});
            fillet(context, id + "F15", {"entities" : qUnion([Q0]), "radius" : 2 * mm, "tangentPropagation" : true, "allowEdgeOverflow" : false});
        }
        {
            var Q0;
            {var subQ0=sQuery(id+"F0.wireOp",EDGE,"E21.filletArc");var subQ1=sQuery(id+"F0.wireOp",EDGE,"E7");var subQ2=sQuery(id+"F0.wireOp",EDGE,"E6");var subQ3=sQuery(id+"F0.wireOp",EDGE,"E5");var subQ4=sQuery(id+"F0.wireOp",EDGE,"E4");var subQ5=sQuery(id+"F0.wireOp",EDGE,"E22.filletArc");var subQ6=sQuery(id+"F0.wireOp",EDGE,"E1.bottom");var subQ7=sQuery(id+"F0.wireOp",EDGE,"E1.right");var subQ8=sQuery(id+"F0.wireOp",EDGE,"E1.top");var subQ9=sQuery(id+"F0.wireOp",EDGE,"E1.left");var subQ10=sQuery(id+"F0.wireOp",EDGE,"E23.filletArc");var subQ11=sQuery(id+"F0.wireOp",EDGE,"E24.filletArc");Q0=makeQuery(id+"F2.boolean.opBoolean","SPLIT",FACE,{"disambiguationData":[TD([makeQuery(id+"F1.opExtrude","SWEPT_FACE",FACE,{"disambiguationData":[OSD([subQ6])]})])],"derivedFrom":makeQuery(id+"F1.opExtrude","CAP_FACE",FACE,{"disambiguationData":[OSD([subQ6,subQ8,subQ9,subQ7,subQ4,subQ3,subQ2,subQ1,subQ0,subQ5,subQ10,subQ11])],"isStart":true})});}
            var sketch = newSketch(context, id + "F16", { "sketchPlane" : qUnion([Q0])});
            skLineSegment(sketch, "E79.0", {"start": v(-70, 90) * mm, "end": v(70, 90) * mm});
            skArc(sketch, "E79.1", {"start": v(80, 80) * mm, "mid": v(77.07, 87.07) * mm, "end": v(70, 90) * mm});
            skLineSegment(sketch, "E79.2", {"start": v(80, -80) * mm, "end": v(80, 80) * mm});
            skArc(sketch, "E79.3", {"start": v(70, -90) * mm, "mid": v(77.07, -87.07) * mm, "end": v(80, -80) * mm});
            skLineSegment(sketch, "E79.4", {"start": v(-70, -90) * mm, "end": v(70, -90) * mm});
            skArc(sketch, "E79.5", {"start": v(-80, -80) * mm, "mid": v(-77.07, -87.07) * mm, "end": v(-70, -90) * mm});
            skLineSegment(sketch, "E79.6", {"start": v(-80, -80) * mm, "end": v(-80, 80) * mm});
            skArc(sketch, "E79.7", {"start": v(-70, 90) * mm, "mid": v(-77.07, 87.07) * mm, "end": v(-80, 80) * mm});
            skCircle(sketch, "E79.8", {"center": v(-60, 67.5) * mm, "radius": 4 * mm});
            skCircle(sketch, "E79.9", {"center": v(60, 67.5) * mm, "radius": 4 * mm});
            skCircle(sketch, "E79.10", {"center": v(60, -67.5) * mm, "radius": 4 * mm});
            skCircle(sketch, "E79.11", {"center": v(-60, -67.5) * mm, "radius": 4 * mm});
            skArc(sketch, "E79.12", {"start": v(56.15, 48.18) * mm, "mid": v(0, 67.5) * mm, "end": v(-56.15, 48.18) * mm});
            skArc(sketch, "E79.13", {"start": v(60, 40.3) * mm, "mid": v(58.99, 44.68) * mm, "end": v(56.15, 48.18) * mm});
            skLineSegment(sketch, "E79.14", {"start": v(60, 40.3) * mm, "end": v(60, -40.3) * mm});
            skArc(sketch, "E79.15", {"start": v(56.15, -48.18) * mm, "mid": v(58.99, -44.68) * mm, "end": v(60, -40.3) * mm});
            skArc(sketch, "E79.16", {"start": v(-56.15, -48.18) * mm, "mid": v(0, -67.5) * mm, "end": v(56.15, -48.18) * mm});
            skLineSegment(sketch, "E79.17", {"start": v(-60, 40.3) * mm, "end": v(-60, -40.3) * mm});
            skArc(sketch, "E79.18", {"start": v(-60, -40.3) * mm, "mid": v(-58.99, -44.68) * mm, "end": v(-56.15, -48.18) * mm});
            skArc(sketch, "E79.19", {"start": v(-56.15, 48.18) * mm, "mid": v(-58.99, 44.68) * mm, "end": v(-60, 40.3) * mm});
            skLineSegment(sketch, "E80", {"start": v(15, 108) * mm, "end": v(33, 90) * mm});
            skLineSegment(sketch, "E81", {"start": v(-15, 108) * mm, "end": v(-15, 120) * mm});
            skLineSegment(sketch, "E82", {"start": v(15, 108) * mm, "end": v(15, 120) * mm});
            skArc(sketch, "E83", {"start": v(15, 120) * mm, "mid": v(0, 135) * mm, "end": v(-15, 120) * mm});
            skLineSegment(sketch, "E84", {"start": v(-15, 108) * mm, "end": v(-33, 90) * mm});
            skCircle(sketch, "E85", {"center": v(0, 120) * mm, "radius": 6 * mm});
            skLineSegment(sketch, "E86", {"start": v(0, 90) * mm, "end": v(0, 120) * mm, "construction": true});
            skLineSegment(sketch, "E87.MirrorCS", {"start": v(-5.75, 0) * mm, "end": v(68.5, 0) * mm, "construction": true});
            skLineSegment(sketch, "E88", {"start": v(-80, 0) * mm, "end": v(68.5, 0) * mm, "construction": true});
            skLineSegment(sketch, "E89.MirrorCS", {"start": v(-15, -108) * mm, "end": v(-33, -90) * mm});
            skLineSegment(sketch, "E90.MirrorCS", {"start": v(-15, -108) * mm, "end": v(-15, -120) * mm});
            skArc(sketch, "E91.MirrorCS", {"start": v(15, -120) * mm, "mid": v(0, -135) * mm, "end": v(-15, -120) * mm});
            skLineSegment(sketch, "E92.MirrorCS", {"start": v(15, -108) * mm, "end": v(33, -90) * mm});
            skLineSegment(sketch, "E93.MirrorCS", {"start": v(15, -108) * mm, "end": v(15, -120) * mm});
            skCircle(sketch, "E94.MirrorC", {"center": v(0, -120) * mm, "radius": 6 * mm});
            skSolve(sketch);
        }
        {
            var Q0;
            Q0 = qSketchRegion(id + "F16", true);
            var Q1;
            Q1=makeQuery(id+"F2.opExtrude","CAP_FACE",FACE,{"disambiguationData":[OSD([sQuery(id+"F0.wireOp",EDGE,"E12"),sQuery(id+"F0.wireOp",EDGE,"E13"),sQuery(id+"F0.wireOp",EDGE,"E14"),sQuery(id+"F0.wireOp",EDGE,"E15"),sQuery(id+"F0.wireOp",EDGE,"E17.filletArc"),sQuery(id+"F0.wireOp",EDGE,"E18.filletArc"),sQuery(id+"F0.wireOp",EDGE,"E19.filletArc"),sQuery(id+"F0.wireOp",EDGE,"E20.filletArc"),sQuery(id+"F0.wireOp",EDGE,"E25.0"),sQuery(id+"F0.wireOp",EDGE,"E25.1"),sQuery(id+"F0.wireOp",EDGE,"E25.2"),sQuery(id+"F0.wireOp",EDGE,"E25.3"),sQuery(id+"F0.wireOp",EDGE,"E25.4"),sQuery(id+"F0.wireOp",EDGE,"E25.5"),sQuery(id+"F0.wireOp",EDGE,"E25.6"),sQuery(id+"F0.wireOp",EDGE,"E25.7")])],"isStart":false});
            extrude(context, id + "F17", {"entities" : qUnion([Q0]), "endBound" : BoundingType.UP_TO_SURFACE, "depth" : 25 * mm, "endBoundEntityFace" : qUnion([Q1]), "offsetDistance" : 25 * mm});
        }
    });
